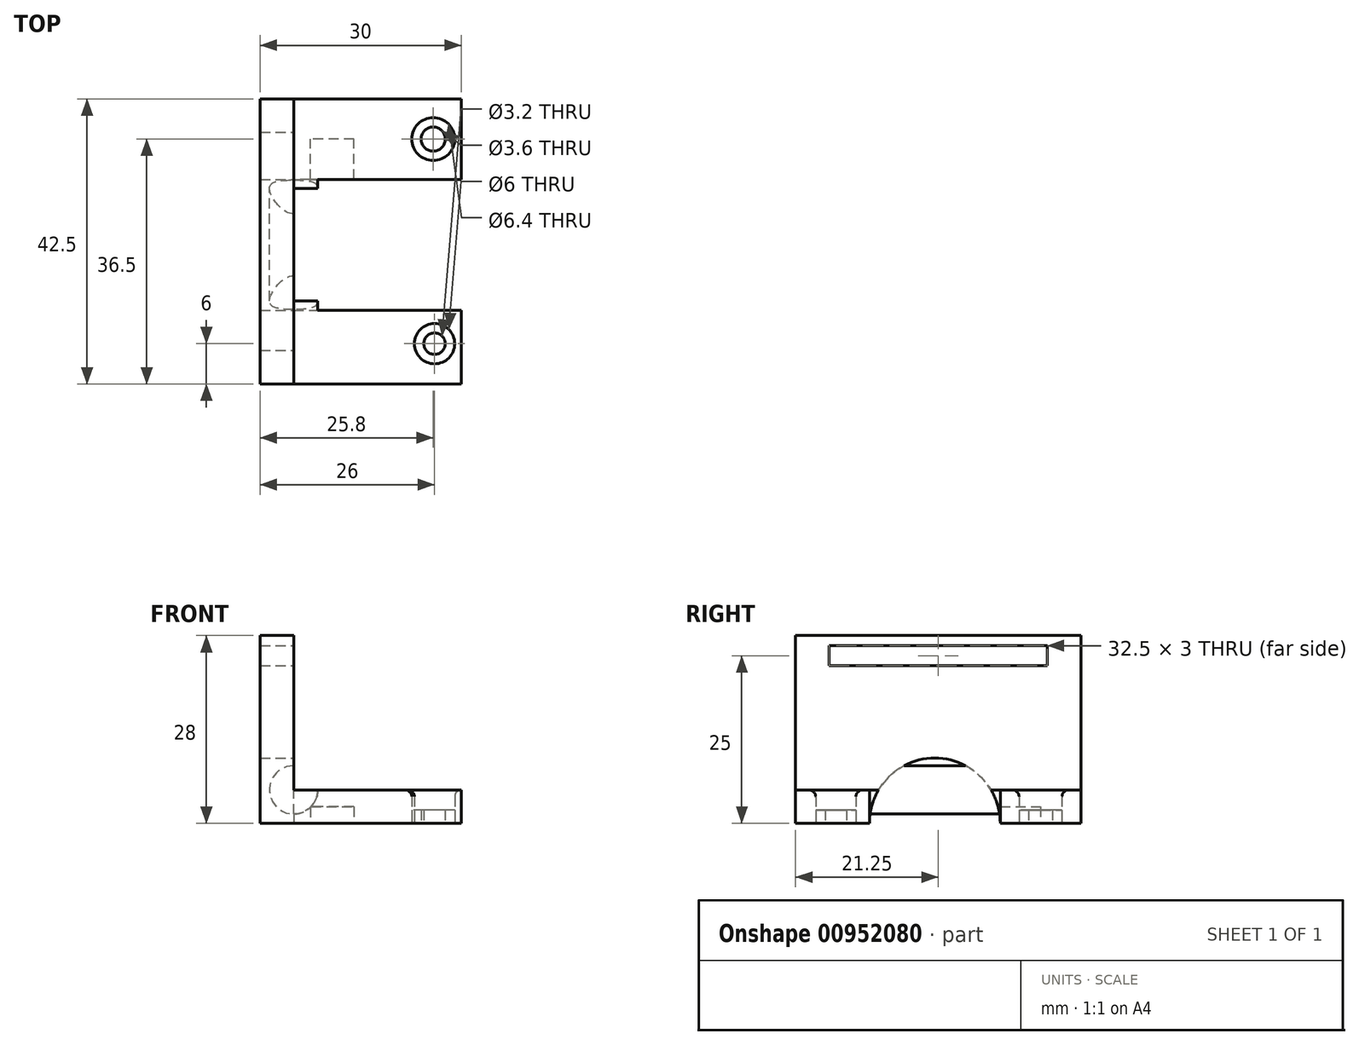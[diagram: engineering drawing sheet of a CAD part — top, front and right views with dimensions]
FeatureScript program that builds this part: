
annotation { "Feature Type Name" : "Feature", "Feature Type Description" : "" }
export const myFeature = defineFeature(function(context is Context, id is Id, definition is map)
    precondition{}
    {
        {
            var Q0;
            Q0=qCreatedBy(makeId("Top.planeOp"),FACE);
            var sketch = newSketch(context, id + "F0", { "sketchPlane" : qUnion([Q0])});
            skLineSegment(sketch, "E0.bottom", {"start": v(0, 0) * mm, "end": v(-25, 0) * mm});
            skLineSegment(sketch, "E0.top", {"start": v(0, 42.5) * mm, "end": v(-25, 42.5) * mm});
            skLineSegment(sketch, "E0.left", {"start": v(0, 0) * mm, "end": v(0, 42.5) * mm});
            skLineSegment(sketch, "E0.right", {"start": v(-25, 0) * mm, "end": v(-25, 42.5) * mm});
            skLineSegment(sketch, "E1.top", {"start": v(0, 11) * mm, "end": v(-25, 11) * mm});
            skLineSegment(sketch, "E1.left", {"start": v(0, 0) * mm, "end": v(0, 11) * mm});
            skLineSegment(sketch, "E1.right", {"start": v(-25, 0) * mm, "end": v(-25, 11) * mm});
            skLineSegment(sketch, "E2.bottom", {"start": v(-25, 42.5) * mm, "end": v(0, 42.5) * mm});
            skLineSegment(sketch, "E2.top", {"start": v(-25, 30.5) * mm, "end": v(0, 30.5) * mm});
            skLineSegment(sketch, "E2.left", {"start": v(-25, 42.5) * mm, "end": v(-25, 30.5) * mm});
            skLineSegment(sketch, "E2.right", {"start": v(0, 42.5) * mm, "end": v(0, 30.5) * mm});
            skCircle(sketch, "E3", {"center": v(-4, 6) * mm, "radius": 3 * mm});
            skCircle(sketch, "E4", {"center": v(-4.2, 36.5) * mm, "radius": 3.2 * mm});
            skCircle(sketch, "E5.0", {"center": v(-4.2, 36.5) * mm, "radius": 1.8 * mm});
            skCircle(sketch, "E6.0", {"center": v(-4, 6) * mm, "radius": 1.6 * mm});
            skSolve(sketch);
        }
        {
            var Q0;
            {var subQ2=sQuery(id+"F0.wireOp",EDGE,"E0.top");Q0=makeQuery(id+"F0.imprint","IMPRINT",FACE,{"disambiguationData":[TD([[makeQuery(id+"F0.imprint","IMPRINT",EDGE,{"derivedFrom":subQ2}),1.0]])]});}
            var Q1;
            {var subQ2=sQuery(id+"F0.wireOp",EDGE,"E0.bottom");Q1=makeQuery(id+"F0.imprint","IMPRINT",FACE,{"disambiguationData":[TD([[makeQuery(id+"F0.imprint","IMPRINT",EDGE,{"derivedFrom":subQ2}),-1.0]])]});}
            extrude(context, id + "F1", {"entities" : qUnion([Q0, Q1]), "depth" : 5 * mm, "offsetDistance" : 25 * mm});
        }
        {
            var Q0;
            {var subQ0=sQuery(id+"F0.wireOp",EDGE,"E0.right");Q0=makeQuery(id+"F1.opExtrude","SWEPT_FACE",FACE,{"disambiguationData":[OSD([subQ0]),TDD([makeQuery(id+"F0.imprint","IMPRINT",EDGE,{"disambiguationData":[TD([[makeQuery(id+"F0.imprint","INTERSECT",VERTEX,{"derivedFrom":[sQuery(id+"F0.wireOp",EDGE,"E0.top"),subQ0]}),1.0]])],"derivedFrom":subQ0})])]});}
            var sketch = newSketch(context, id + "F2", { "sketchPlane" : qUnion([Q0])});
            skLineSegment(sketch, "E7.bottom", {"start": v(0, 0) * mm, "end": v(-42.5, 0) * mm});
            skLineSegment(sketch, "E7.top", {"start": v(0, 28) * mm, "end": v(-42.5, 28) * mm});
            skLineSegment(sketch, "E7.left", {"start": v(0, 0) * mm, "end": v(0, 28) * mm});
            skLineSegment(sketch, "E7.right", {"start": v(-42.5, 0) * mm, "end": v(-42.5, 28) * mm});
            skLineSegment(sketch, "E8.bottom", {"start": v(-5, 26.5) * mm, "end": v(-37.5, 26.5) * mm});
            skLineSegment(sketch, "E8.top", {"start": v(-5, 23.5) * mm, "end": v(-37.5, 23.5) * mm});
            skLineSegment(sketch, "E8.left", {"start": v(-5, 26.5) * mm, "end": v(-5, 23.5) * mm});
            skLineSegment(sketch, "E8.right", {"start": v(-37.5, 26.5) * mm, "end": v(-37.5, 23.5) * mm});
            skCircle(sketch, "E9", {"center": v(-20.75, 0) * mm, "radius": 9.75 * mm});
            skSolve(sketch);
        }
        {
            var Q0;
            {var subQ3=sQuery(id+"F2.wireOp",EDGE,"E7.top");Q0=makeQuery(id+"F2.imprint","IMPRINT",FACE,{"disambiguationData":[TD([[makeQuery(id+"F2.imprint","IMPRINT",EDGE,{"derivedFrom":subQ3}),1.0]])]});}
            var Q1;
            {var subQ3=sQuery(id+"F0.wireOp",EDGE,"E2.top");var subQ4=sQuery(id+"F0.wireOp",EDGE,"E0.right");var subQ5=makeQuery(id+"F1.opExtrude","SWEPT_EDGE",EDGE,{"disambiguationData":[OSD([subQ4,subQ3])]});Q1=makeQuery(id+"F2.imprint","IMPRINT",FACE,{"disambiguationData":[TD([[makeQuery(id+"F2.imprint","IMPRINT",EDGE,{"derivedFrom":subQ5}),-1.0]])]});}
            extrude(context, id + "F3", {"entities" : qUnion([Q0, Q1]), "operationType" : NewBodyOperationType.ADD, "depth" : 5 * mm, "offsetDistance" : 25 * mm});
        }
        {
            var Q0;
            Q0=makeQuery(id+"F3.opExtrude","SWEPT_FACE",FACE,{"disambiguationData":[OSD([sQuery(id+"F2.wireOp",EDGE,"E7.right")])]});
            var sketch = newSketch(context, id + "F4", { "sketchPlane" : qUnion([Q0])});
            skCircle(sketch, "E10", {"center": v(25, 5) * mm, "radius": 3.6 * mm});
            skSolve(sketch);
        }
        {
            var Q0;
            {var subQ0=sQuery(id+"F4.wireOp",EDGE,"E10");var subQ1=makeQuery(id+"F3.opExtrude","CAP_EDGE",EDGE,{"disambiguationData":[OSD([sQuery(id+"F2.wireOp",EDGE,"E7.right")])],"isStart":true});var subQ2=makeQuery(id+"F4.imprint","INTERSECT",VERTEX,{"disambiguationData":[OD(0.0)],"derivedFrom":[subQ1,subQ0]});Q0=makeQuery(id+"F4.imprint","IMPRINT",FACE,{"disambiguationData":[TD([[makeQuery(id+"F4.imprint","IMPRINT",EDGE,{"disambiguationData":[TD([[subQ2,1.0]])],"derivedFrom":subQ0}),1.0]])]});}
            var Q1;
            Q1=makeQuery(id+"F3.boolean.opBoolean","MERGE",FACE,{"derivedFrom":[makeQuery(id+"F1.opExtrude","SWEPT_FACE",FACE,{"disambiguationData":[OSD([sQuery(id+"F0.wireOp",EDGE,"E0.bottom")])]}),makeQuery(id+"F3.opExtrude","SWEPT_FACE",FACE,{"disambiguationData":[OSD([sQuery(id+"F2.wireOp",EDGE,"E7.left")])]})]});
            extrude(context, id + "F5", {"entities" : qUnion([Q0]), "operationType" : NewBodyOperationType.ADD, "endBound" : BoundingType.UP_TO_SURFACE, "oppositeDirection" : true, "depth" : 36.5 * mm, "endBoundEntityFace" : qUnion([Q1]), "offsetDistance" : 25 * mm});
        }
        {
            var Q0;
            Q0=makeQuery(id+"F1.opExtrude","CAP_FACE",FACE,{"disambiguationData":[OSD([sQuery(id+"F0.wireOp",EDGE,"E0.top"),sQuery(id+"F0.wireOp",EDGE,"E0.left"),sQuery(id+"F0.wireOp",EDGE,"E0.right"),sQuery(id+"F0.wireOp",EDGE,"E2.top"),sQuery(id+"F0.wireOp",EDGE,"E4")])],"isStart":true});
            var sketch = newSketch(context, id + "F6", { "sketchPlane" : qUnion([Q0])});
            skLineSegment(sketch, "E11.bottom", {"start": v(-16, -30.5) * mm, "end": v(-22.5, -30.5) * mm});
            skLineSegment(sketch, "E11.top", {"start": v(-16, -36.5) * mm, "end": v(-22.5, -36.5) * mm});
            skLineSegment(sketch, "E11.left", {"start": v(-16, -30.5) * mm, "end": v(-16, -36.5) * mm});
            skLineSegment(sketch, "E11.right", {"start": v(-22.5, -30.5) * mm, "end": v(-22.5, -36.5) * mm});
            skSolve(sketch);
        }
        {
            var Q0;
            Q0=makeQuery(id+"F6.imprint","IMPRINT",FACE,{"disambiguationData":[TD([[makeQuery(id+"F6.imprint","IMPRINT",EDGE,{"derivedFrom":sQuery(id+"F6.wireOp",EDGE,"E11.bottom")}),-1.0]])]});
            extrude(context, id + "F7", {"entities" : qUnion([Q0]), "operationType" : NewBodyOperationType.REMOVE, "oppositeDirection" : true, "depth" : 2.5 * mm, "offsetDistance" : 25 * mm});
        }
        {
            var Q0;
            {var subQ0=sQuery(id+"F2.wireOp",EDGE,"E9");var subQ1=sQuery(id+"F2.wireOp",EDGE,"E7.bottom");var subQ3=makeQuery(id+"F2.imprint","INTERSECT",VERTEX,{"derivedFrom":[subQ1,subQ0]});Q0=makeQuery(id+"F2.imprint","IMPRINT",FACE,{"disambiguationData":[TD([[makeQuery(id+"F2.imprint","IMPRINT",EDGE,{"disambiguationData":[TD([[subQ3,-1.0]])],"derivedFrom":subQ1}),-1.0]])]});}
            extrude(context, id + "F8", {"entities" : qUnion([Q0]), "operationType" : NewBodyOperationType.REMOVE, "oppositeDirection" : true, "depth" : 25 * mm, "offsetDistance" : 25 * mm});
        }
        {
            var Q0;
            Q0=makeQuery(id+"F0.imprint","IMPRINT",FACE,{"disambiguationData":[TD([[makeQuery(id+"F0.imprint","IMPRINT",EDGE,{"derivedFrom":sQuery(id+"F0.wireOp",EDGE,"E3")}),1.0]])]});
            var Q1;
            Q1=makeQuery(id+"F0.imprint","IMPRINT",FACE,{"disambiguationData":[TD([[makeQuery(id+"F0.imprint","IMPRINT",EDGE,{"derivedFrom":sQuery(id+"F0.wireOp",EDGE,"E4")}),1.0]])]});
            extrude(context, id + "F9", {"entities" : qUnion([Q0, Q1]), "depth" : 2 * mm, "offsetDistance" : 25 * mm});
        }
        {
            var Q0;
            Q0=makeQuery(id+"F1.opExtrude","CAP_EDGE",EDGE,{"disambiguationData":[OSD([sQuery(id+"F0.wireOp",EDGE,"E3")])],"isStart":false});
            var Q1;
            Q1=makeQuery(id+"F1.opExtrude","CAP_EDGE",EDGE,{"disambiguationData":[OSD([sQuery(id+"F0.wireOp",EDGE,"E4")])],"isStart":false});
            fillet(context, id + "F10", {"entities" : qUnion([Q0, Q1]), "radius" : 1 * mm, "tangentPropagation" : true, "allowEdgeOverflow" : false});
        }
    });
